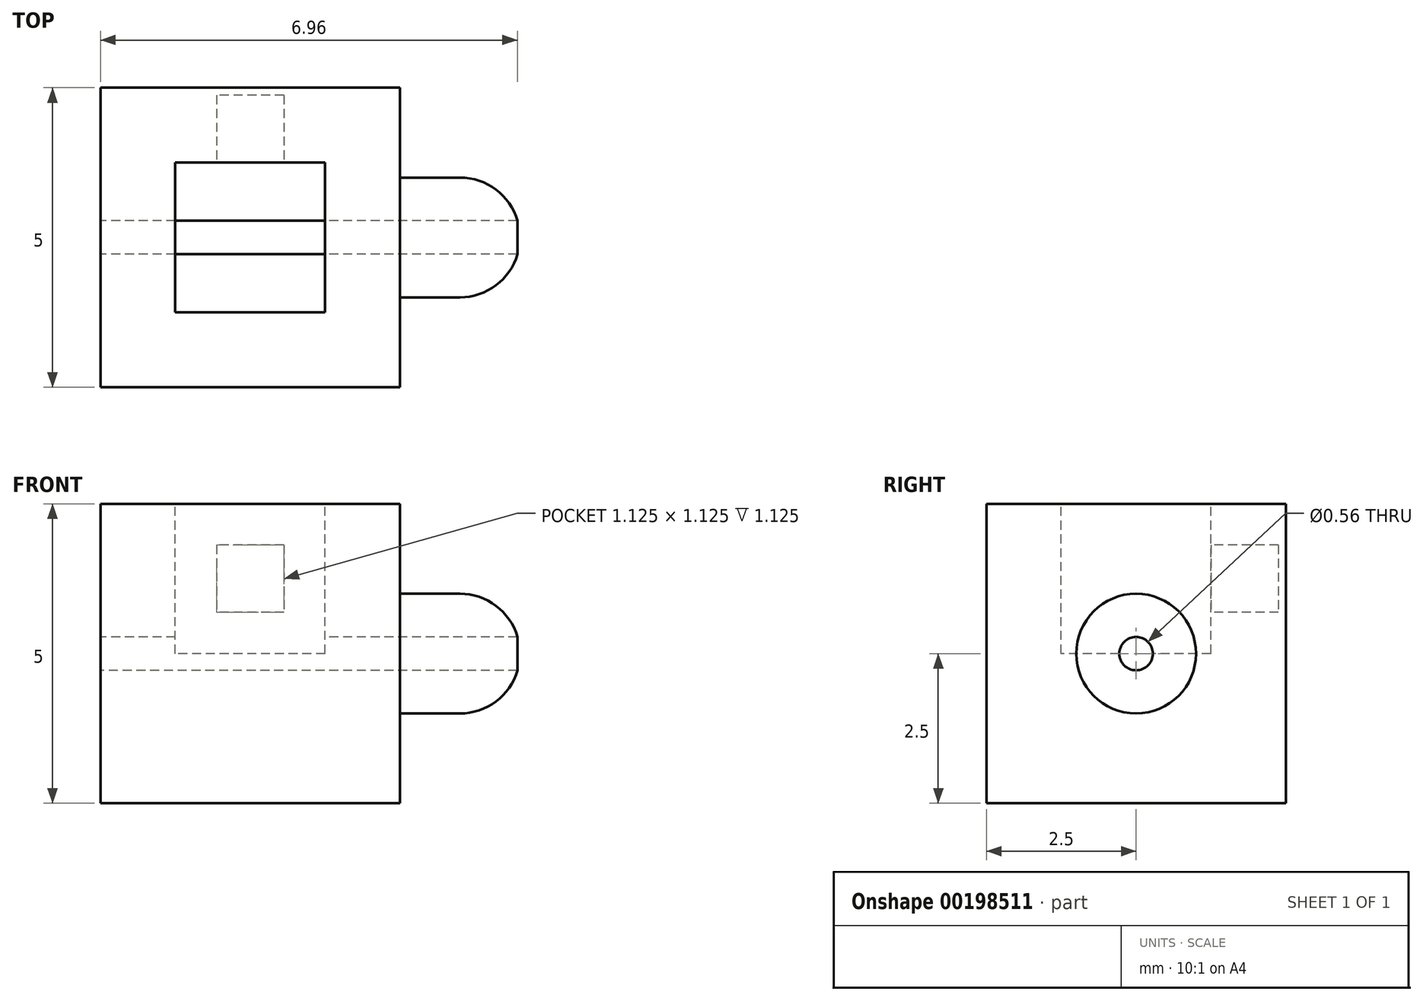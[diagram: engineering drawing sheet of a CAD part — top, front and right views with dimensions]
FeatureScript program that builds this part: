
annotation { "Feature Type Name" : "Feature", "Feature Type Description" : "" }
export const myFeature = defineFeature(function(context is Context, id is Id, definition is map)
    precondition{}
    {
        {
            var Q0;
            Q0=qCreatedBy(makeId("Top.planeOp"),FACE);
            var sketch = newSketch(context, id + "F0", { "sketchPlane" : qUnion([Q0])});
            skLineSegment(sketch, "E0.bottom", {"start": v(0, 0) * mm, "end": v(-5, 0) * mm});
            skLineSegment(sketch, "E0.top", {"start": v(0, -5) * mm, "end": v(-5, -5) * mm});
            skLineSegment(sketch, "E0.left", {"start": v(0, 0) * mm, "end": v(0, -5) * mm});
            skLineSegment(sketch, "E0.right", {"start": v(-5, 0) * mm, "end": v(-5, -5) * mm});
            skLineSegment(sketch, "E1.bottom", {"start": v(0, 0) * mm, "end": v(5, 0) * mm, "construction": true});
            skLineSegment(sketch, "E1.top", {"start": v(0, 5) * mm, "end": v(5, 5) * mm, "construction": true});
            skLineSegment(sketch, "E1.left", {"start": v(0, 0) * mm, "end": v(0, 5) * mm, "construction": true});
            skLineSegment(sketch, "E1.right", {"start": v(5, 0) * mm, "end": v(5, 5) * mm, "construction": true});
            skLineSegment(sketch, "E2.bottom", {"start": v(0, 0) * mm, "end": v(5, 0) * mm});
            skLineSegment(sketch, "E2.top", {"start": v(0, -5) * mm, "end": v(5, -5) * mm});
            skLineSegment(sketch, "E2.right", {"start": v(5, 0) * mm, "end": v(5, -5) * mm});
            skSolve(sketch);
        }
        {
            var Q0;
            Q0=makeQuery(id+"F0.imprint","IMPRINT",FACE,{"disambiguationData":[TD([[makeQuery(id+"F0.imprint","IMPRINT",EDGE,{"derivedFrom":sQuery(id+"F0.wireOp",EDGE,"E2.bottom")}),-1.0]])]});
            var Q1;
            Q1=sQuery(id+"F0.wireOp",EDGE,"E0.bottom");
            var Q2;
            Q2=sQuery(id+"F0.wireOp",EDGE,"E0.top");
            var Q3;
            Q3=sQuery(id+"F0.wireOp",EDGE,"E0.right");
            var Q4;
            Q4=sQuery(id+"F0.wireOp",EDGE,"E0.left");
            extrude(context, id + "F1", {"entities" : qUnion([Q0]), "bodyType" : ToolBodyType.SURFACE, "surfaceEntities" : qUnion([Q1, Q2, Q3, Q4]), "oppositeDirection" : true, "depth" : 5 * mm});
        }
        {
            var Q0;
            Q0=makeQuery(id+"F0.imprint","IMPRINT",FACE,{"disambiguationData":[TD([[makeQuery(id+"F0.imprint","IMPRINT",EDGE,{"derivedFrom":sQuery(id+"F0.wireOp",EDGE,"E2.bottom")}),-1.0]])]});
            extrude(context, id + "F2", {"entities" : qUnion([Q0]), "depth" : 5 * mm});
        }
        {
            var Q0;
            Q0=makeQuery(id+"F2.opExtrude","CAP_FACE",FACE,{"disambiguationData":[OSD([sQuery(id+"F0.wireOp",EDGE,"E2.bottom"),sQuery(id+"F0.wireOp",EDGE,"E2.top"),sQuery(id+"F0.wireOp",EDGE,"E0.left"),sQuery(id+"F0.wireOp",EDGE,"E2.right")])],"isStart":false});
            var sketch = newSketch(context, id + "F3", { "sketchPlane" : qUnion([Q0])});
            skLineSegment(sketch, "E3", {"start": v(5, -5) * mm, "end": v(0, 0) * mm, "construction": true});
            skLineSegment(sketch, "E4", {"start": v(0, -5) * mm, "end": v(5, 0) * mm, "construction": true});
            skLineSegment(sketch, "E5.bottom", {"start": v(3.75, -1.25) * mm, "end": v(1.25, -1.25) * mm});
            skLineSegment(sketch, "E5.top", {"start": v(3.75, -3.75) * mm, "end": v(1.25, -3.75) * mm});
            skLineSegment(sketch, "E5.left", {"start": v(3.75, -1.25) * mm, "end": v(3.75, -3.75) * mm});
            skLineSegment(sketch, "E5.right", {"start": v(1.25, -1.25) * mm, "end": v(1.25, -3.75) * mm});
            skPoint(sketch, "E5.middle", {"position": v(2.5, -2.5) * mm});
            skSolve(sketch);
        }
        {
            var Q0;
            Q0=makeQuery(id+"F3.imprint","IMPRINT",FACE,{"disambiguationData":[TD([[makeQuery(id+"F3.imprint","IMPRINT",EDGE,{"derivedFrom":sQuery(id+"F3.wireOp",EDGE,"E5.bottom")}),1.0]])]});
            extrude(context, id + "F4", {"entities" : qUnion([Q0]), "operationType" : NewBodyOperationType.REMOVE, "oppositeDirection" : true, "depth" : 2.5 * mm});
        }
        {
            var Q0;
            Q0=makeQuery(id+"F4.boolean.opBoolean","COPY",FACE,{"derivedFrom":makeQuery(id+"F4.opExtrude","SWEPT_FACE",FACE,{"disambiguationData":[OSD([sQuery(id+"F3.wireOp",EDGE,"E5.bottom")])]})});
            var sketch = newSketch(context, id + "F5", { "sketchPlane" : qUnion([Q0])});
            skLineSegment(sketch, "E6", {"start": v(1.25, 5) * mm, "end": v(3.75, 2.5) * mm, "construction": true});
            skLineSegment(sketch, "E7", {"start": v(3.75, 5) * mm, "end": v(1.25, 2.5) * mm, "construction": true});
            skLineSegment(sketch, "E8.bottom", {"start": v(3.06, 4.31) * mm, "end": v(1.94, 4.31) * mm});
            skLineSegment(sketch, "E8.top", {"start": v(3.06, 3.19) * mm, "end": v(1.94, 3.19) * mm});
            skLineSegment(sketch, "E8.left", {"start": v(3.06, 4.31) * mm, "end": v(3.06, 3.19) * mm});
            skLineSegment(sketch, "E8.right", {"start": v(1.94, 4.31) * mm, "end": v(1.94, 3.19) * mm});
            skPoint(sketch, "E8.middle", {"position": v(2.5, 3.75) * mm});
            skSolve(sketch);
        }
        {
            var Q0;
            Q0 = qSketchRegion(id + "F5", true);
            extrude(context, id + "F6", {"entities" : qUnion([Q0]), "operationType" : NewBodyOperationType.REMOVE, "oppositeDirection" : true, "depth" : 1.12 * mm});
        }
        {
            var Q0;
            Q0=makeQuery(id+"F2.opExtrude","SWEPT_FACE",FACE,{"disambiguationData":[OSD([sQuery(id+"F0.wireOp",EDGE,"E2.right")])]});
            var sketch = newSketch(context, id + "F7", { "sketchPlane" : qUnion([Q0])});
            skLineSegment(sketch, "E9", {"start": v(-5, 5) * mm, "end": v(0, 0) * mm, "construction": true});
            skLineSegment(sketch, "E10", {"start": v(0, 5) * mm, "end": v(-5, 0) * mm, "construction": true});
            skCircle(sketch, "E11", {"center": v(-2.5, 2.5) * mm, "radius": 1 * mm});
            skSolve(sketch);
        }
        {
            var Q0;
            Q0 = qSketchRegion(id + "F7", true);
            extrude(context, id + "F8", {"entities" : qUnion([Q0]), "operationType" : NewBodyOperationType.ADD, "depth" : 1 * mm});
        }
        {
            var Q0;
            Q0=makeQuery(id+"F8.opExtrude","CAP_FACE",FACE,{"disambiguationData":[OSD([sQuery(id+"F7.wireOp",EDGE,"E11")])],"isStart":false});
            var sketch = newSketch(context, id + "F9", { "sketchPlane" : qUnion([Q0])});
            skLineSegment(sketch, "E12", {"start": v(-2.5, 2.5) * mm, "end": v(-2.5, 3.5) * mm, "construction": true});
            skLineSegment(sketch, "E13", {"start": v(-2.5, 3.5) * mm, "end": v(-2.5, 1.5) * mm});
            skSolve(sketch);
        }
        {
            var Q0;
            {var subQ0=sQuery(id+"F9.wireOp",EDGE,"E13");Q0=makeQuery(id+"F9.imprint","IMPRINT",FACE,{"disambiguationData":[TD([[makeQuery(id+"F9.imprint","IMPRINT",EDGE,{"derivedFrom":subQ0}),1.0]])]});}
            var Q1;
            Q1=sQuery(id+"F9.wireOp",EDGE,"E13");
            revolve(context, id + "F10", {"operationType" : NewBodyOperationType.ADD, "entities" : qUnion([Q0]), "axis" : qUnion([Q1]), "revolveType" : RevolveType.ONE_DIRECTION, "angle" : 180 * degree});
        }
        {
            var Q0;
            Q0=makeQuery(id+"F2.opExtrude","SWEPT_FACE",FACE,{"disambiguationData":[OSD([sQuery(id+"F0.wireOp",EDGE,"E2.right")])]});
            var sketch = newSketch(context, id + "F11", { "sketchPlane" : qUnion([Q0])});
            skLineSegment(sketch, "E14", {"start": v(-5, 5) * mm, "end": v(0, 0) * mm, "construction": true});
            skLineSegment(sketch, "E15", {"start": v(-5, 0) * mm, "end": v(0, 5) * mm, "construction": true});
            skLineSegment(sketch, "E16", {"start": v(-1.8, 3.2) * mm, "end": v(-1.21, 3.79) * mm, "construction": true});
            skCircle(sketch, "E17", {"center": v(-2.5, 2.5) * mm, "radius": 0.28 * mm});
            skSolve(sketch);
        }
        {
            var Q0;
            Q0 = qSketchRegion(id + "F11", true);
            extrude(context, id + "F12", {"entities" : qUnion([Q0]), "operationType" : NewBodyOperationType.REMOVE, "depth" : 25.4 * mm});
        }
        {
            var Q0;
            Q0 = qSketchRegion(id + "F11", true);
            extrude(context, id + "F13", {"entities" : qUnion([Q0]), "operationType" : NewBodyOperationType.REMOVE, "depth" : 2 * mm, "hasSecondDirection" : true, "secondDirectionOppositeDirection" : true, "secondDirectionDepth" : 5 * mm});
        }
    });
